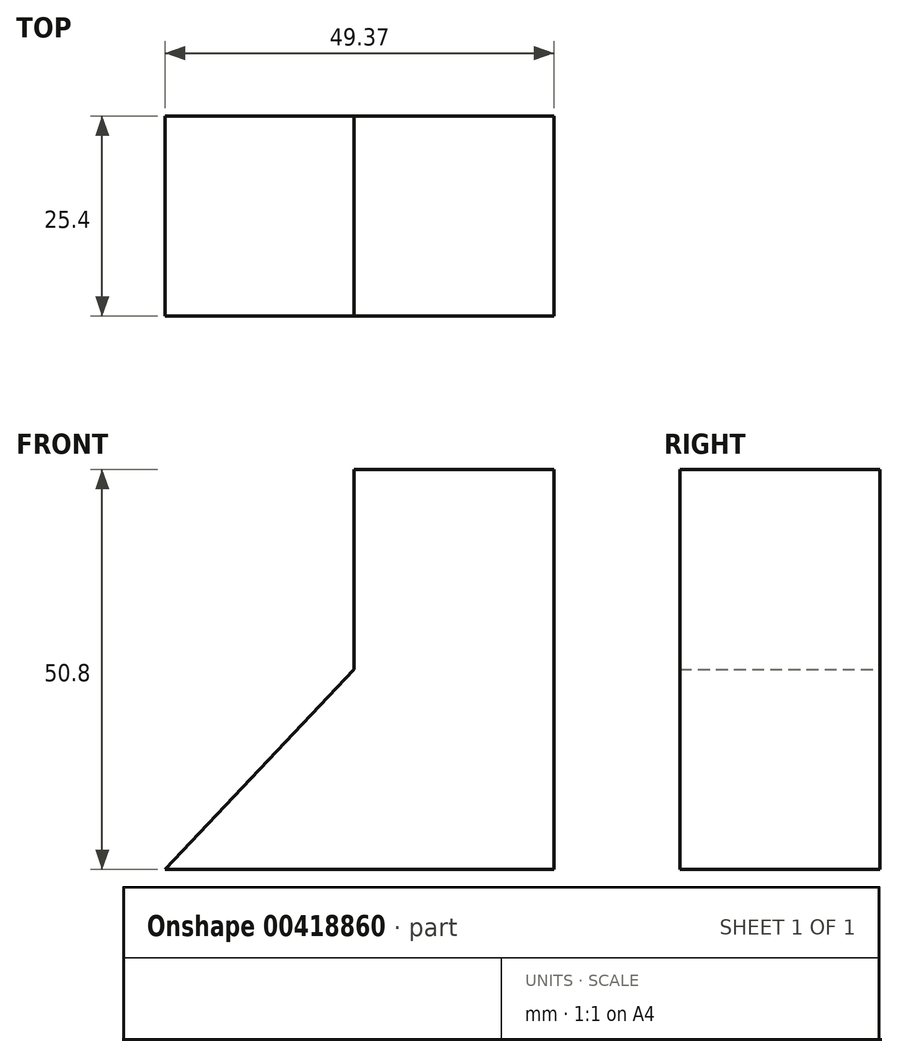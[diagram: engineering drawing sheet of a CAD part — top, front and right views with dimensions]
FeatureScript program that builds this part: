
annotation { "Feature Type Name" : "Feature", "Feature Type Description" : "" }
export const myFeature = defineFeature(function(context is Context, id is Id, definition is map)
    precondition{}
    {
        {
            var Q0;
            Q0=qCreatedBy(makeId("Front.planeOp"),FACE);
            var sketch = newSketch(context, id + "F0", { "sketchPlane" : qUnion([Q0])});
            skLineSegment(sketch, "E0", {"start": v(0, 0) * mm, "end": v(50.8, 0) * mm});
            skLineSegment(sketch, "E1", {"start": v(50.8, 0) * mm, "end": v(50.8, 50.8) * mm});
            skLineSegment(sketch, "E2", {"start": v(50.8, 50.8) * mm, "end": v(25.4, 50.8) * mm});
            skLineSegment(sketch, "E3", {"start": v(25.4, 50.8) * mm, "end": v(25.4, 25.4) * mm});
            skLineSegment(sketch, "E4", {"start": v(25.4, 25.4) * mm, "end": v(0, -1.52) * mm});
            skLineSegment(sketch, "E5", {"start": v(0, -1.52) * mm, "end": v(-125.02, 80.01) * mm});
            skSolve(sketch);
        }
        {
            var Q0;
            Q0 = qSketchRegion(id + "F0", true);
            extrude(context, id + "F1", {"entities" : qUnion([Q0]), "depth" : 25.4 * mm});
        }
    });
